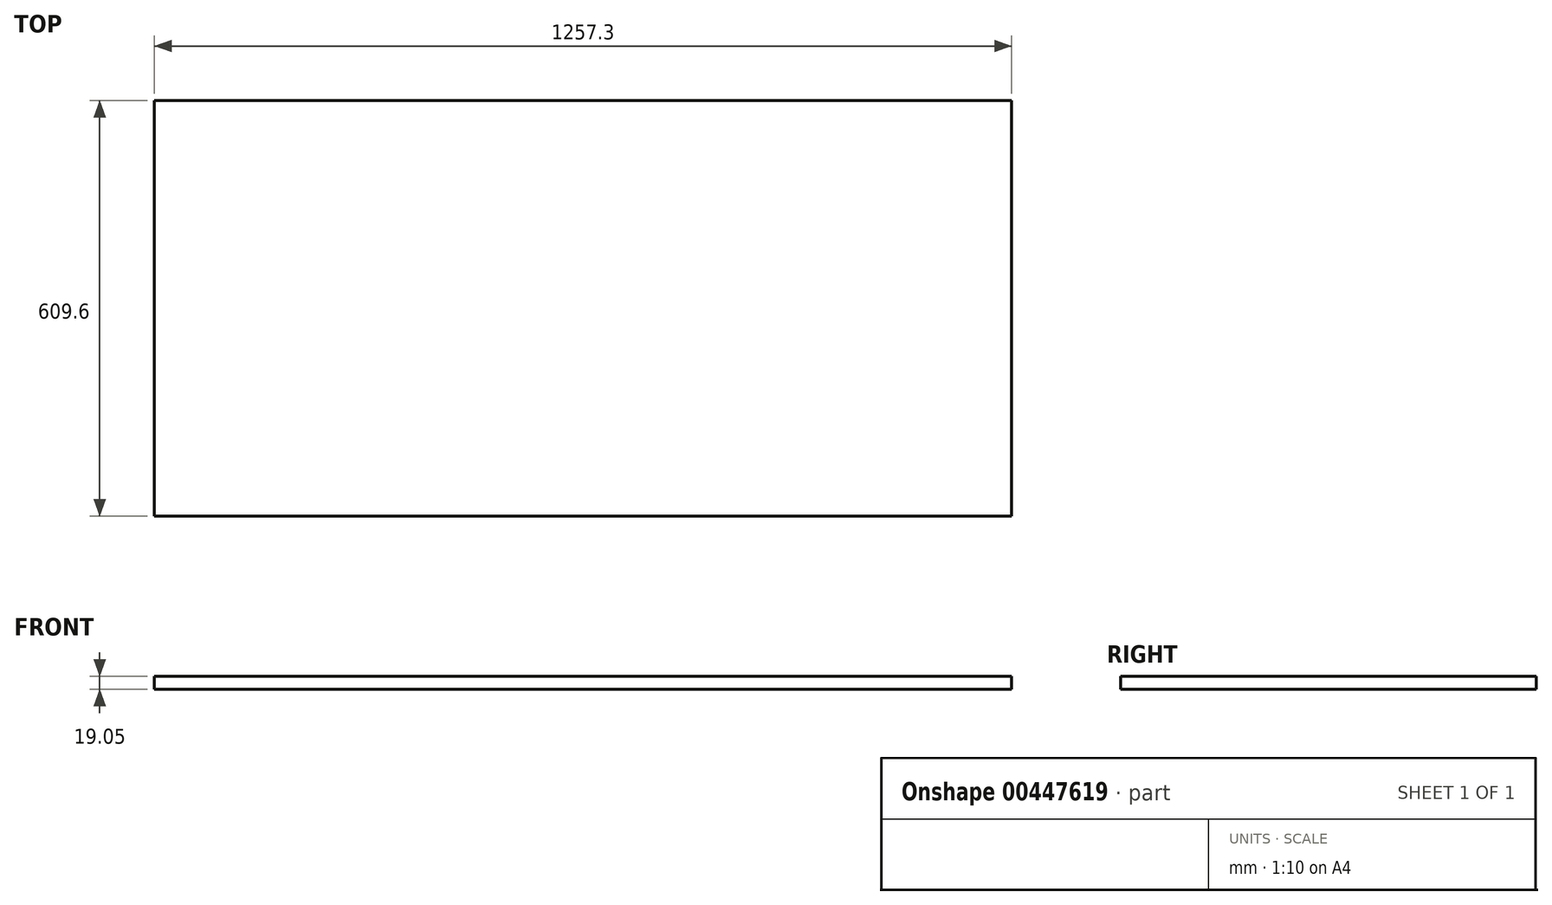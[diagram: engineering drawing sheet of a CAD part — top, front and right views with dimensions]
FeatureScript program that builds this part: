
annotation { "Feature Type Name" : "Feature", "Feature Type Description" : "" }
export const myFeature = defineFeature(function(context is Context, id is Id, definition is map)
    precondition{}
    {
        {
            var Q0;
            Q0=qCreatedBy(makeId("Top.planeOp"),FACE);
            var sketch = newSketch(context, id + "F0", { "sketchPlane" : qUnion([Q0])});
            skLineSegment(sketch, "E0.bottom", {"start": v(0, 0) * mm, "end": v(1257.3, 0) * mm});
            skLineSegment(sketch, "E0.top", {"start": v(0, 609.6) * mm, "end": v(1257.3, 609.6) * mm});
            skLineSegment(sketch, "E0.left", {"start": v(0, 0) * mm, "end": v(0, 609.6) * mm});
            skLineSegment(sketch, "E0.right", {"start": v(1257.3, 0) * mm, "end": v(1257.3, 609.6) * mm});
            skSolve(sketch);
        }
        {
            var Q0;
            Q0 = qSketchRegion(id + "F0", true);
            extrude(context, id + "F1", {"entities" : qUnion([Q0]), "depth" : 19.05 * mm, "offsetDistance" : 25.4 * mm});
        }
    });
